# Revit family: LWplc_Latchwaysplc_BaluAndGuardSym_VersiRail_Fixed
name_source: partatom
category: Railings
revit_build: Autodesk Revit 2013 (Build: 20121003_2115(x64)
units: mm (PartAtom-declared; Revit-internal decimal feet)

## types (6) — shared parameters
AssetType = Fixed
BracketMaterial = LWplc_Latchwaysplc_Aluminium_Polished
Default Elevation = 1219 mm
Description = Latchways ManSafe VersiRail
Diameter = 40 mm  [stored 0.131234 ft]
DurationUnit = year
Height = 1150 mm
IfcExportAs = GUARDRAIL
IfcExportType = IfcRailing
IsExternal = Yes
ManufacturerName = Latchways plc
ManufacturerURL = www.latchways.com
Material = Handrails & Uprights: Aluminium
NBSDescription = Balustrade and guarding system
NBSReference = 25-25-10/110
NominalHeight = 1150 mm
PostHeight = 10 mm  [stored 0.0328084 ft]
RailMaterial = LWplc_Latchwaysplc_Aluminium_Polished
URL = www.latchways.com
Uniclass2 = Ss_25_15_60_05
UprightLength = 1150 mm
Version = 1
WarrantyDurationUnit = year
zero-valued in all types: PostBaseGap

## per-type parameters (varying)
| type | BIMObjectName | BasePlateVis | Model | ModelNumber | ModelReference | NominalLength | NominalWidth | ParapetCurvedUpright | ParapetInclinedUpright | ParapetStraightUpright | ProductInformation | Size | WallCurvedUpright | WallInclinedUpright | WallMountVis | WallStraightUpright |
| BalustradeAndGuardingSystem_VersiRailFixed_WallMountCurved_Latchwaysplc | LWplc_Latchwaysplc_BalustradeAndGuardingSystem_VersiRailFixed_WallMountCurved | No | 22228-00+22042-00 | 22228-00+22042-00 | VersiRail - Wall Mounted Curved Fixed assembly | 596 mm  [stored 1.95538 ft] | 110 mm  [stored 0.360892 ft] | No | No | No | www.latchways.com/BIM/Latchways_WallMountedCurvedVersiRail_Datasheet.pdf | 110 x 596 x 1150 mm | Yes | No | Yes | No |
| BalustradeAndGuardingSystem_VersiRailFixed_WallMountInclined_Latchwaysplc | LWplc_Latchwaysplc_BalustradeAndGuardingSystem_VersiRailFixed_WallMountInclined | No | 22228-00+22042-00 | 22120-00+22042-00 | VersiRail - Wall Mounted Inclined Fixed assembly | 450 mm  [stored 1.47638 ft] | 110 mm  [stored 0.360892 ft] | No | No | No | www.latchways.com/BIM/Latchways_WallMountedInclinedVersiRail_Datasheet.pdf | 110 x 450 x 1150 mm | No | Yes | Yes | No |
| BalustradeAndGuardingSystem_VersiRailFixed_WallMountStraight_Latchwaysplc | LWplc_Latchwaysplc_BalustradeAndGuardingSystem_VersiRailFixed_WallMountStraight | No | 22028-00+22042-00 | 22028-00+22042-00 | VersiRail - Wall Mounted Straight Fixed assembly | 120 mm  [stored 0.393701 ft] | 110 mm  [stored 0.360892 ft] | No | No | No | www.latchways.com/BIM/Latchways_WallMountedStraightVersiRail_Datasheet.pdf | 110 x 120 x 1150 mm | No | No | Yes | Yes |
| BalustradeAndGuardingSystem_VersiRailFixed_SlabAndParapetStraight_Latchwaysplc | LWplc_Latchwaysplc_BalustradeAndGuardingSystem_VersiRailFixed_SlabAndParapetStraight | Yes | 22028-00+22044-00 | 22028-00+22044-00 | VersiRail - Slab And Parapet Mounted Straight Fixed assembly | 120 mm  [stored 0.393701 ft] | 186 mm  [stored 0.610236 ft] | No | No | Yes | www.latchways.com/BIM/Latchways_Parapet-SlabMounted_StraightVersiRail_Datasheet.pdf | 186 x 120 x 1150 mm | No | No | No | No |
| BalustradeAndGuardingSystem_VersiRailFixed_SlabAndParapetInclined_Latchwaysplc | LWplc_Latchwaysplc_BalustradeAndGuardingSystem_VersiRailFixed_SlabAndParapetInclined | Yes | 22120-00+22044-00 | 22120-00+22044-00 | VersiRail - Slab And Parapet Mounted Inclined Fixed assembly | 325 mm  [stored 1.06627 ft] | 186 mm  [stored 0.610236 ft] | No | Yes | No | www.latchways.com/BIM/Latchways_Parapet-SlabMounted_InclinedVersiRail_Datasheet.pdf | 186 x 325 x 1150 mm | No | No | No | No |
| BalustradeAndGuardingSystem_VersiRailFixed_SlabAndParapetCurved_Latchwaysplc | LWplc_Latchwaysplc_BalustradeAndGuardingSystem_VersiRailFixed_SlabAndParapetCurved | Yes | 22120-00+22044-00 | 22228-00+22044-00 | VersiRail - Slab And Parapet Mounted Curved Fixed assembly | 440 mm  [stored 1.44357 ft] | 186 mm  [stored 0.610236 ft] | Yes | No | No | www.latchways.com/BIM/Latchways_Parapet-SlabMounted_CurvedVersiRail_Datasheet.pdf | 186 x 440 x 1150 mm | No | No | No | No |

note: column(s) folded — value = type name in every type: Name

note: [stored X ft] marks values corroborated as IEEE doubles in the binary element streams (Revit-internal decimal feet)

## geometry (parser evidence)
native form markers: Blend x6, Sweep x8
no freeform markers — native parametric forms only
